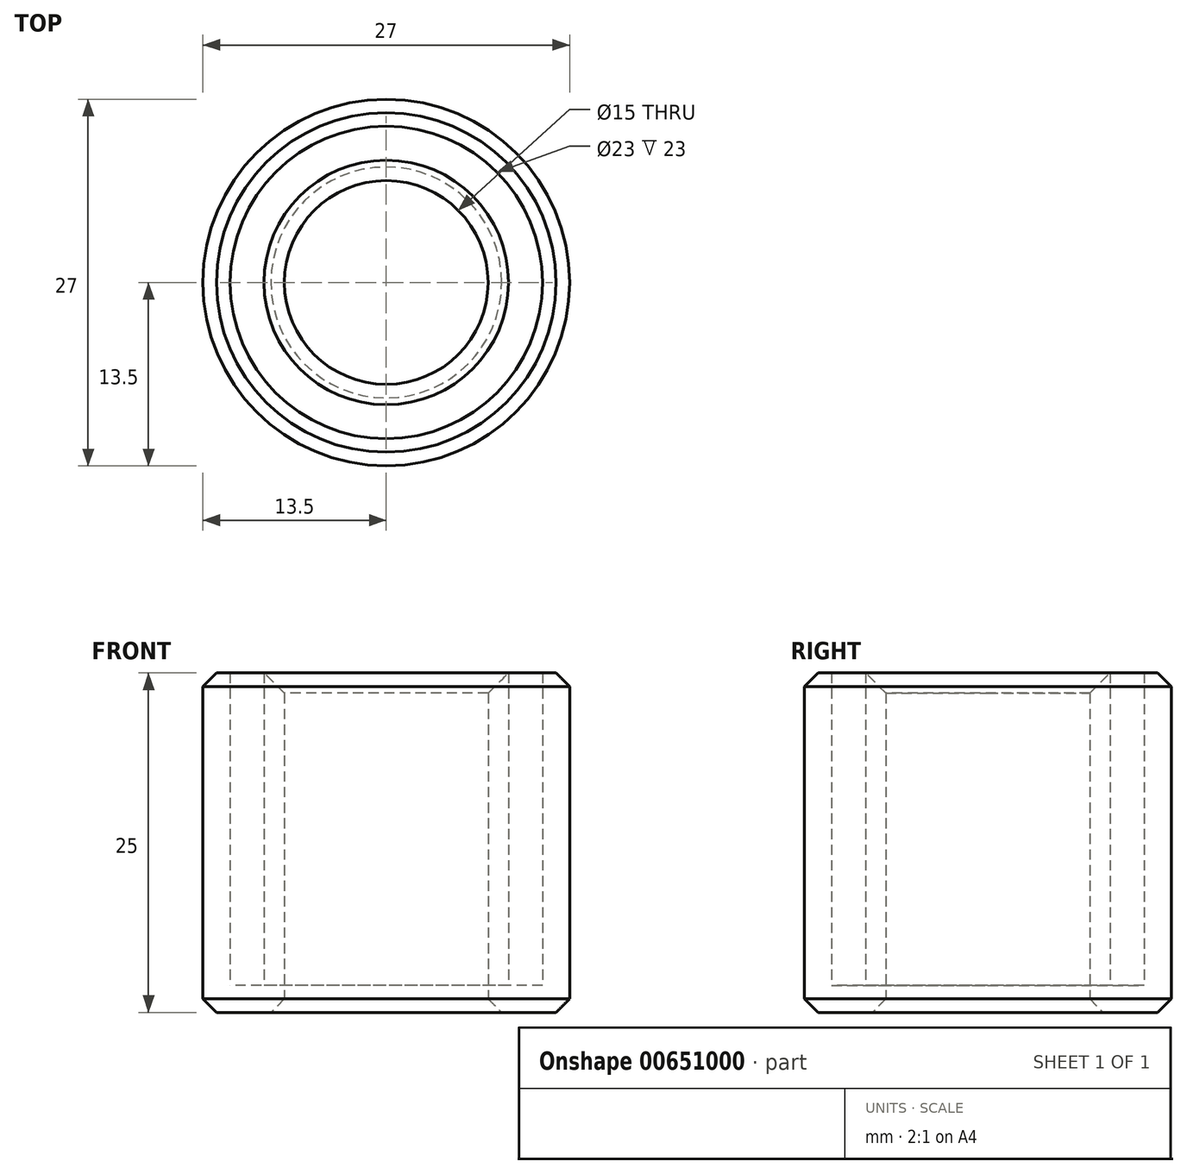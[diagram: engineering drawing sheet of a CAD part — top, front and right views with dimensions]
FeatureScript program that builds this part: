
annotation { "Feature Type Name" : "Feature", "Feature Type Description" : "" }
export const myFeature = defineFeature(function(context is Context, id is Id, definition is map)
    precondition{}
    {
        {
            assignVariable(context, id + "F0", {"name" : "Base", "anyValue" : 2});
        }
        {
            assignVariable(context, id + "F1", {"name" : "Outer_height", "anyValue" : 25});
        }
        {
            var Q0;
            Q0=qCreatedBy(makeId("Top.planeOp"),FACE);
            var sketch = newSketch(context, id + "F2", { "sketchPlane" : qUnion([Q0])});
            skCircle(sketch, "E0", {"center": v(0, 0) * mm, "radius": 7.5 * mm});
            skCircle(sketch, "E1", {"center": v(0, 0) * mm, "radius": 9 * mm});
            skCircle(sketch, "E2", {"center": v(0, 0) * mm, "radius": 11.5 * mm});
            skCircle(sketch, "E3", {"center": v(0, 0) * mm, "radius": 13.5 * mm});
            skSolve(sketch);
        }
        {
            var Q0;
            Q0=makeQuery(id+"F2.imprint","IMPRINT",FACE,{"disambiguationData":[TD([[makeQuery(id+"F2.imprint","IMPRINT",EDGE,{"derivedFrom":sQuery(id+"F2.wireOp",EDGE,"E1")}),-1.0]])]});
            var Q1;
            Q1=makeQuery(id+"F2.imprint","IMPRINT",FACE,{"disambiguationData":[TD([[makeQuery(id+"F2.imprint","IMPRINT",EDGE,{"derivedFrom":sQuery(id+"F2.wireOp",EDGE,"E2")}),-1.0]])]});
            var Q2;
            Q2=makeQuery(id+"F2.imprint","IMPRINT",FACE,{"disambiguationData":[TD([[makeQuery(id+"F2.imprint","IMPRINT",EDGE,{"derivedFrom":sQuery(id+"F2.wireOp",EDGE,"E0")}),-1.0]])]});
            extrude(context, id + "F3", {"entities" : qUnion([Q0, Q1, Q2]), "depth" : getVariable(context, 'Base') * mm, "offsetDistance" : 25 * mm});
        }
        {
            var Q0;
            Q0=makeQuery(id+"F2.imprint","IMPRINT",FACE,{"disambiguationData":[TD([[makeQuery(id+"F2.imprint","IMPRINT",EDGE,{"derivedFrom":sQuery(id+"F2.wireOp",EDGE,"E0")}),-1.0]])]});
            var Q1;
            Q1=makeQuery(id+"F2.imprint","IMPRINT",FACE,{"disambiguationData":[TD([[makeQuery(id+"F2.imprint","IMPRINT",EDGE,{"derivedFrom":sQuery(id+"F2.wireOp",EDGE,"E2")}),-1.0]])]});
            extrude(context, id + "F4", {"entities" : qUnion([Q0, Q1]), "operationType" : NewBodyOperationType.ADD, "depth" : getVariable(context, 'Outer_height') * mm, "offsetDistance" : 25 * mm});
        }
        {
            var Q0;
            Q0=makeQuery(id+"F4.opExtrude","CAP_EDGE",EDGE,{"disambiguationData":[OSD([sQuery(id+"F2.wireOp",EDGE,"E0")])],"isStart":false});
            chamfer(context, id + "F5", {"entities" : qUnion([Q0]), "width" : 1.5 * mm, "tangentPropagation" : true});
        }
        {
            var Q0;
            Q0=makeQuery(id+"F4.opExtrude","CAP_EDGE",EDGE,{"disambiguationData":[OSD([sQuery(id+"F2.wireOp",EDGE,"E3")])],"isStart":false});
            var Q1;
            Q1=makeQuery(id+"F3.opExtrude","CAP_EDGE",EDGE,{"disambiguationData":[OSD([sQuery(id+"F2.wireOp",EDGE,"E3")])],"isStart":true});
            var Q2;
            Q2=makeQuery(id+"F3.opExtrude","CAP_EDGE",EDGE,{"disambiguationData":[OSD([sQuery(id+"F2.wireOp",EDGE,"E0")])],"isStart":true});
            chamfer(context, id + "F6", {"entities" : qUnion([Q0, Q1, Q2]), "width" : 1 * mm, "tangentPropagation" : true});
        }
    });
